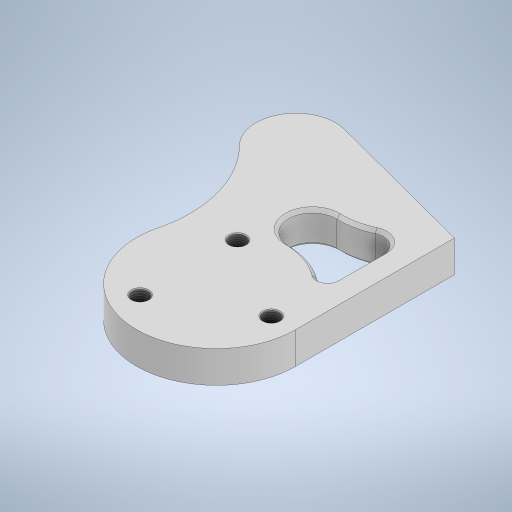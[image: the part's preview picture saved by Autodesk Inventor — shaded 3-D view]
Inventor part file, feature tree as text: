
AUTODESK INVENTOR PART (.ipt)
format: ipt  version: 2023.2 (Build 272271000, 271)  size: 297,984 bytes
history: native  units: mm
features: thread x3, chamfer x2, extrude x1, sketch x1
ambient origin geometry x8: Origin, YZ Plane, XZ Plane, XY Plane, X Axis, Y Axis, Z Axis, Center Point
bodies: Body1 (feature_tree)
feature tree (7):
  extrude  "Extrusion2"  Depth=50.0mm
  chamfer  "Chamfer2"  Distance=50.0mm
  chamfer  "Chamfer3"  Distance=75.0mm
  thread  "Thread1"  [1 undecoded]
  thread  "Thread2"  [1 undecoded]
  thread  "Thread3"  [1 undecoded]
  sketch  "Sketch1"  dims[d0=100.0mm d3=50.0mm d5=50.0mm d6=75.0mm d13=15.0mm d14=60.0mm d16=45.0mm d17=5.0mm d19=10.0mm d24=30.0mm d25=15.0mm d26=45.0mm d57=10.0mm d58=35.0mm d59=30.0mm d61=360.0deg d63=20.0mm d64=0.0mm d65=2.0mm d66=2.0mm d67=45.0deg d68=0.5mm d69=2.0mm d70=45.0deg d71=19.5mm d72=0.0mm d73=19.5mm d74=0.0mm d75=19.5mm d76=0.0mm]
note: 3 required parameter values undecoded (feature->parameter linkage not recoverable at this tier; creation-order binding heuristic only, values carry confidence <= 0.55)
